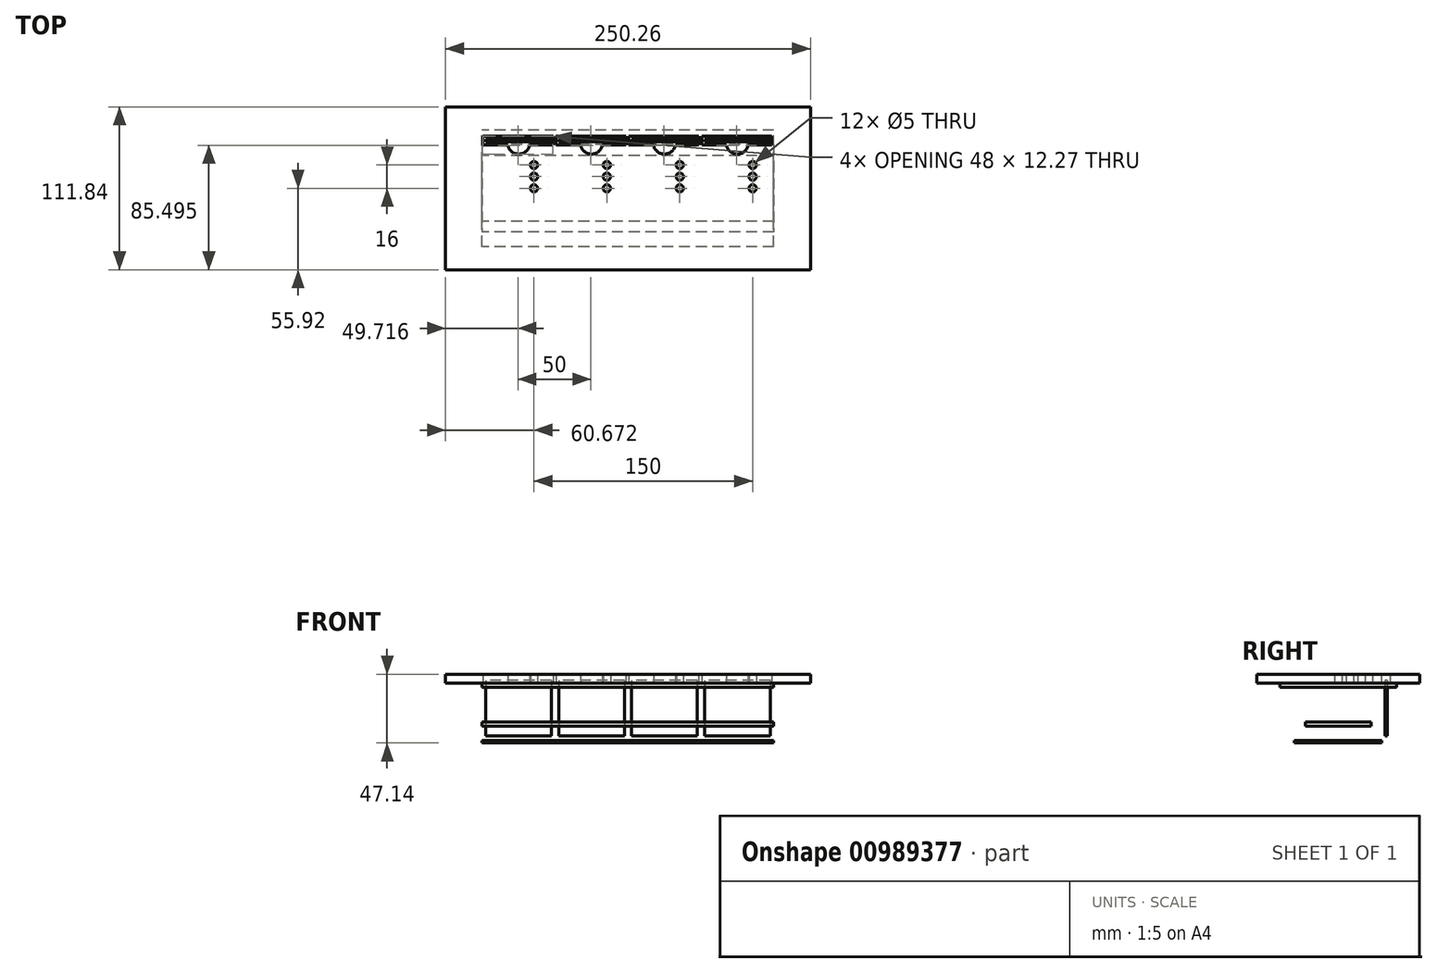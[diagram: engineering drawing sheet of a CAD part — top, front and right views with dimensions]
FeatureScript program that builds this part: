
annotation { "Feature Type Name" : "Feature", "Feature Type Description" : "" }
export const myFeature = defineFeature(function(context is Context, id is Id, definition is map)
    precondition{}
    {
        {
            var Q0;
            Q0=qCreatedBy(makeId("Top.planeOp"),FACE);
            var sketch = newSketch(context, id + "F0", { "sketchPlane" : qUnion([Q0])});
            skLineSegment(sketch, "E0.bottom", {"start": v(100, 30) * mm, "end": v(-100, 30) * mm});
            skLineSegment(sketch, "E0.top", {"start": v(100, -30) * mm, "end": v(-100, -30) * mm});
            skLineSegment(sketch, "E0.left", {"start": v(100, 30) * mm, "end": v(100, -30) * mm});
            skLineSegment(sketch, "E0.right", {"start": v(-100, 30) * mm, "end": v(-100, -30) * mm});
            skPoint(sketch, "E0.middle", {"position": v(0, 0) * mm});
            skSolve(sketch);
        }
        {
            var Q0;
            Q0 = qSketchRegion(id + "F0", true);
            extrude(context, id + "F1", {"entities" : qUnion([Q0]), "depth" : 1.6 * mm, "offsetDistance" : 25 * mm});
        }
        {
            var Q0;
            Q0=qCreatedBy(makeId("Top.planeOp"),FACE);
            var sketch = newSketch(context, id + "F2", { "sketchPlane" : qUnion([Q0])});
            skLineSegment(sketch, "E1.bottom", {"start": v(-52.5, 33.6) * mm, "end": v(-97.5, 33.6) * mm});
            skLineSegment(sketch, "E1.top", {"start": v(-52.5, 32) * mm, "end": v(-97.5, 32) * mm});
            skLineSegment(sketch, "E1.left", {"start": v(-52.5, 33.6) * mm, "end": v(-52.5, 32) * mm});
            skLineSegment(sketch, "E1.right", {"start": v(-97.5, 33.6) * mm, "end": v(-97.5, 32) * mm});
            skPoint(sketch, "E1.middle", {"position": v(-75, 32.8) * mm});
            skLineSegment(sketch, "E2.1.0.0", {"start": v(-2.5, 32) * mm, "end": v(-47.5, 32) * mm});
            skPoint(sketch, "E2.1.0.1", {"position": v(-25, 32.8) * mm});
            skLineSegment(sketch, "E2.1.0.2", {"start": v(-2.5, 33.6) * mm, "end": v(-47.5, 33.6) * mm});
            skLineSegment(sketch, "E2.1.0.3", {"start": v(-2.5, 33.6) * mm, "end": v(-2.5, 32) * mm});
            skLineSegment(sketch, "E2.1.0.4", {"start": v(-47.5, 33.6) * mm, "end": v(-47.5, 32) * mm});
            skLineSegment(sketch, "E2.2.0.0", {"start": v(47.5, 32) * mm, "end": v(2.5, 32) * mm});
            skPoint(sketch, "E2.2.0.1", {"position": v(25, 32.8) * mm});
            skLineSegment(sketch, "E2.2.0.2", {"start": v(47.5, 33.6) * mm, "end": v(2.5, 33.6) * mm});
            skLineSegment(sketch, "E2.2.0.3", {"start": v(47.5, 33.6) * mm, "end": v(47.5, 32) * mm});
            skLineSegment(sketch, "E2.2.0.4", {"start": v(2.5, 33.6) * mm, "end": v(2.5, 32) * mm});
            skLineSegment(sketch, "E2.3.0.0", {"start": v(97.5, 32) * mm, "end": v(52.5, 32) * mm});
            skPoint(sketch, "E2.3.0.1", {"position": v(75, 32.8) * mm});
            skLineSegment(sketch, "E2.3.0.2", {"start": v(97.5, 33.6) * mm, "end": v(52.5, 33.6) * mm});
            skLineSegment(sketch, "E2.3.0.3", {"start": v(97.5, 33.6) * mm, "end": v(97.5, 32) * mm});
            skLineSegment(sketch, "E2.3.0.4", {"start": v(52.5, 33.6) * mm, "end": v(52.5, 32) * mm});
            skLineSegment(sketch, "E2.direction1", {"start": v(-97.5, 32) * mm, "end": v(-47.5, 32) * mm, "construction": true});
            skSolve(sketch);
        }
        {
            var Q0;
            Q0 = qSketchRegion(id + "F2", true);
            extrude(context, id + "F3", {"entities" : qUnion([Q0]), "depth" : 43 * mm, "offsetDistance" : 25 * mm, "hasSecondDirection" : true, "secondDirectionOppositeDirection" : false, "secondDirectionDepth" : 5 * mm});
        }
        {
            var Q0;
            Q0=qCreatedBy(makeId("Right.planeOp"),FACE);
            var sketch = newSketch(context, id + "F4", { "sketchPlane" : qUnion([Q0])});
            skLineSegment(sketch, "E3.bottom", {"start": v(-22.5, 14.44) * mm, "end": v(22.5, 14.44) * mm});
            skLineSegment(sketch, "E3.top", {"start": v(-22.5, 11.44) * mm, "end": v(22.5, 11.44) * mm});
            skLineSegment(sketch, "E3.left", {"start": v(-22.5, 14.44) * mm, "end": v(-22.5, 11.44) * mm});
            skLineSegment(sketch, "E3.right", {"start": v(22.5, 14.44) * mm, "end": v(22.5, 11.44) * mm});
            skPoint(sketch, "E3.middle", {"position": v(0, 12.94) * mm});
            skLineSegment(sketch, "E4.bottom", {"start": v(-40, 38.14) * mm, "end": v(40, 38.14) * mm});
            skLineSegment(sketch, "E4.top", {"start": v(-40, 41.14) * mm, "end": v(40, 41.14) * mm});
            skLineSegment(sketch, "E4.left", {"start": v(-40, 38.14) * mm, "end": v(-40, 41.14) * mm});
            skLineSegment(sketch, "E4.right", {"start": v(40, 38.14) * mm, "end": v(40, 41.14) * mm});
            skPoint(sketch, "E4.middle", {"position": v(0, 39.64) * mm});
            skSolve(sketch);
        }
        {
            var Q0;
            Q0 = qSketchRegion(id + "F4", true);
            extrude(context, id + "F5", {"entities" : qUnion([Q0]), "depth" : 100 * mm, "offsetDistance" : 25 * mm, "hasSecondDirection" : true, "secondDirectionOppositeDirection" : true, "secondDirectionDepth" : 100 * mm});
        }
        {
            var Q0;
            Q0=makeQuery(id+"F5.opExtrude","SWEPT_FACE",FACE,{"disambiguationData":[OSD([sQuery(id+"F4.wireOp",EDGE,"E4.top")])]});
            var sketch = newSketch(context, id + "F6", { "sketchPlane" : qUnion([Q0])});
            skLineSegment(sketch, "E5.bottom", {"start": v(125.13, 55.92) * mm, "end": v(-125.13, 55.92) * mm});
            skLineSegment(sketch, "E5.top", {"start": v(125.13, -55.92) * mm, "end": v(-125.13, -55.92) * mm});
            skLineSegment(sketch, "E5.left", {"start": v(125.13, 55.92) * mm, "end": v(125.13, -55.92) * mm});
            skLineSegment(sketch, "E5.right", {"start": v(-125.13, 55.92) * mm, "end": v(-125.13, -55.92) * mm});
            skPoint(sketch, "E5.middle", {"position": v(0, 0) * mm});
            skLineSegment(sketch, "E6.bottom", {"start": v(-51.41, 35.71) * mm, "end": v(-99.41, 35.71) * mm});
            skLineSegment(sketch, "E6.top", {"start": v(-51.41, 29.71) * mm, "end": v(-67.5, 29.71) * mm});
            skLineSegment(sketch, "E6.left", {"start": v(-51.41, 35.71) * mm, "end": v(-51.41, 29.71) * mm});
            skLineSegment(sketch, "E6.right", {"start": v(-99.41, 35.71) * mm, "end": v(-99.41, 29.71) * mm});
            skPoint(sketch, "E6.middle", {"position": v(-75.41, 32.71) * mm});
            skArc(sketch, "E7", {"start": v(-82.5, 29.71) * mm, "mid": v(-75, 23.44) * mm, "end": v(-67.5, 29.71) * mm});
            skLineSegment(sketch, "E8.trimOffspring", {"start": v(-82.5, 29.71) * mm, "end": v(-99.41, 29.71) * mm});
            skLineSegment(sketch, "E9.1.0.0", {"start": v(-1.41, 29.71) * mm, "end": v(-17.5, 29.71) * mm});
            skLineSegment(sketch, "E9.1.0.1", {"start": v(-1.41, 35.71) * mm, "end": v(-1.41, 29.71) * mm});
            skLineSegment(sketch, "E9.1.0.2", {"start": v(-32.5, 29.71) * mm, "end": v(-49.41, 29.71) * mm});
            skArc(sketch, "E9.1.0.3", {"start": v(-32.5, 29.71) * mm, "mid": v(-25, 23.44) * mm, "end": v(-17.5, 29.71) * mm});
            skPoint(sketch, "E9.1.0.4", {"position": v(-25.41, 32.71) * mm});
            skLineSegment(sketch, "E9.1.0.5", {"start": v(-49.41, 35.71) * mm, "end": v(-49.41, 29.71) * mm});
            skLineSegment(sketch, "E9.1.0.6", {"start": v(-1.41, 35.71) * mm, "end": v(-49.41, 35.71) * mm});
            skLineSegment(sketch, "E9.2.0.0", {"start": v(48.59, 29.71) * mm, "end": v(32.5, 29.71) * mm});
            skLineSegment(sketch, "E9.2.0.1", {"start": v(48.59, 35.71) * mm, "end": v(48.59, 29.71) * mm});
            skLineSegment(sketch, "E9.2.0.2", {"start": v(17.5, 29.71) * mm, "end": v(0.59, 29.71) * mm});
            skArc(sketch, "E9.2.0.3", {"start": v(17.5, 29.71) * mm, "mid": v(25, 23.44) * mm, "end": v(32.5, 29.71) * mm});
            skPoint(sketch, "E9.2.0.4", {"position": v(24.59, 32.71) * mm});
            skLineSegment(sketch, "E9.2.0.5", {"start": v(0.59, 35.71) * mm, "end": v(0.59, 29.71) * mm});
            skLineSegment(sketch, "E9.2.0.6", {"start": v(48.59, 35.71) * mm, "end": v(0.59, 35.71) * mm});
            skLineSegment(sketch, "E9.3.0.0", {"start": v(98.59, 29.71) * mm, "end": v(82.5, 29.71) * mm});
            skLineSegment(sketch, "E9.3.0.1", {"start": v(98.59, 35.71) * mm, "end": v(98.59, 29.71) * mm});
            skLineSegment(sketch, "E9.3.0.2", {"start": v(67.5, 29.71) * mm, "end": v(50.59, 29.71) * mm});
            skArc(sketch, "E9.3.0.3", {"start": v(67.5, 29.71) * mm, "mid": v(75, 23.44) * mm, "end": v(82.5, 29.71) * mm});
            skPoint(sketch, "E9.3.0.4", {"position": v(74.59, 32.71) * mm});
            skLineSegment(sketch, "E9.3.0.5", {"start": v(50.59, 35.71) * mm, "end": v(50.59, 29.71) * mm});
            skLineSegment(sketch, "E9.3.0.6", {"start": v(98.59, 35.71) * mm, "end": v(50.59, 35.71) * mm});
            skLineSegment(sketch, "E9.direction1", {"start": v(-99.41, 29.71) * mm, "end": v(-49.41, 29.71) * mm, "construction": true});
            skCircle(sketch, "E10", {"center": v(-64.46, 0) * mm, "radius": 2.5 * mm});
            skCircle(sketch, "E11.0.1.0", {"center": v(-64.46, 8) * mm, "radius": 2.5 * mm});
            skCircle(sketch, "E11.0.2.0", {"center": v(-64.46, 16) * mm, "radius": 2.5 * mm});
            skCircle(sketch, "E11.1.0.0", {"center": v(-14.46, 0) * mm, "radius": 2.5 * mm});
            skCircle(sketch, "E11.1.1.0", {"center": v(-14.46, 8) * mm, "radius": 2.5 * mm});
            skCircle(sketch, "E11.1.2.0", {"center": v(-14.46, 16) * mm, "radius": 2.5 * mm});
            skCircle(sketch, "E11.2.0.0", {"center": v(35.54, 0) * mm, "radius": 2.5 * mm});
            skCircle(sketch, "E11.2.1.0", {"center": v(35.54, 8) * mm, "radius": 2.5 * mm});
            skCircle(sketch, "E11.2.2.0", {"center": v(35.54, 16) * mm, "radius": 2.5 * mm});
            skCircle(sketch, "E11.3.0.0", {"center": v(85.54, 0) * mm, "radius": 2.5 * mm});
            skCircle(sketch, "E11.3.1.0", {"center": v(85.54, 8) * mm, "radius": 2.5 * mm});
            skCircle(sketch, "E11.3.2.0", {"center": v(85.54, 16) * mm, "radius": 2.5 * mm});
            skLineSegment(sketch, "E11.direction1", {"start": v(-64.46, 0) * mm, "end": v(-14.46, 0) * mm, "construction": true});
            skLineSegment(sketch, "E11.direction2", {"start": v(-64.46, 0) * mm, "end": v(-64.46, 8) * mm, "construction": true});
            skSolve(sketch);
        }
        {
            var Q0;
            Q0 = qSketchRegion(id + "F6", true);
            extrude(context, id + "F7", {"entities" : qUnion([Q0]), "depth" : 6 * mm, "offsetDistance" : 25 * mm});
        }
    });
